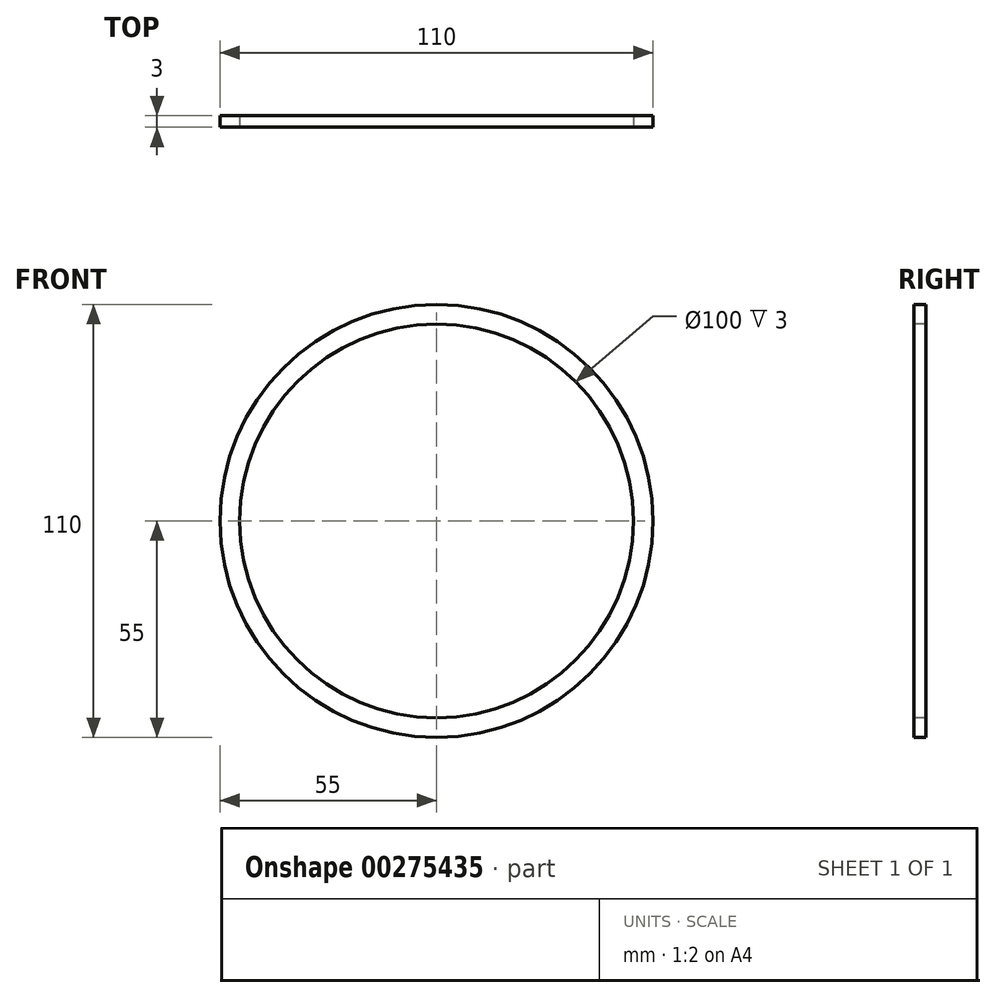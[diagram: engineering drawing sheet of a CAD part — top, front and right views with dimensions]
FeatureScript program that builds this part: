
annotation { "Feature Type Name" : "Feature", "Feature Type Description" : "" }
export const myFeature = defineFeature(function(context is Context, id is Id, definition is map)
    precondition{}
    {
        {
            var Q0;
            Q0=qCreatedBy(makeId("Front.planeOp"),FACE);
            var sketch = newSketch(context, id + "F0", { "sketchPlane" : qUnion([Q0])});
            skCircle(sketch, "E0", {"center": v(0, 0) * mm, "radius": 55 * mm});
            skSolve(sketch);
        }
        {
            var Q0;
            Q0 = qSketchRegion(id + "F0", true);
            var Q1;
            Q1 = qConstructionFilter(qBodyType(qCreatedBy(id + "F0" ,EDGE), BodyType.WIRE), ConstructionObject.NO);
            extrude(context, id + "F1", {"entities" : qUnion([Q0]), "surfaceEntities" : qUnion([Q1]), "depth" : 3 * mm, "offsetDistance" : 25 * mm});
        }
        {
            var Q0;
            Q0=makeQuery(id+"F1.opExtrude","CAP_FACE",FACE,{"disambiguationData":[OSD([sQuery(id+"F0.wireOp",EDGE,"E0")])],"isStart":false});
            var sketch = newSketch(context, id + "F2", { "sketchPlane" : qUnion([Q0])});
            skCircle(sketch, "E1", {"center": v(0, 0) * mm, "radius": 50 * mm});
            skSolve(sketch);
        }
        {
            var Q0;
            Q0 = qSketchRegion(id + "F2", true);
            extrude(context, id + "F3", {"entities" : qUnion([Q0]), "operationType" : NewBodyOperationType.REMOVE, "oppositeDirection" : true, "depth" : 25 * mm, "offsetDistance" : 25 * mm});
        }
    });
